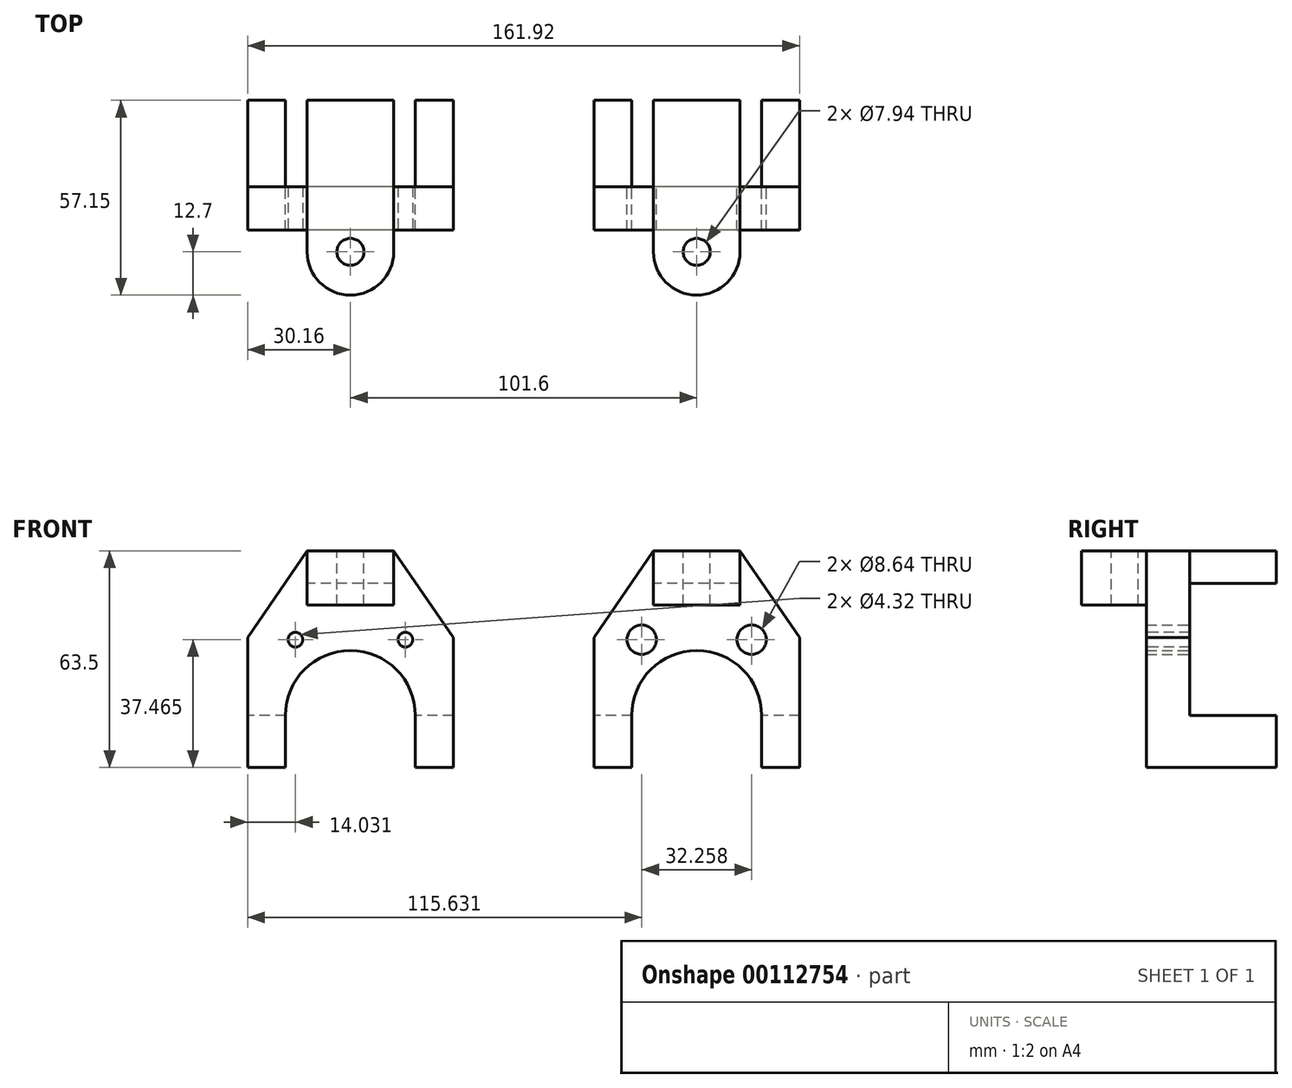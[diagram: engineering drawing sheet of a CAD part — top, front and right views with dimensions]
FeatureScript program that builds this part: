
annotation { "Feature Type Name" : "Feature", "Feature Type Description" : "" }
export const myFeature = defineFeature(function(context is Context, id is Id, definition is map)
    precondition{}
    {
        {
            var Q0;
            Q0=qCreatedBy(makeId("Front.planeOp"),FACE);
            var sketch = newSketch(context, id + "F0", { "sketchPlane" : qUnion([Q0])});
            skLineSegment(sketch, "E0.bottom", {"start": v(30.16, -31.75) * mm, "end": v(19.05, -31.75) * mm});
            skLineSegment(sketch, "E0.top", {"start": v(12.7, 31.75) * mm, "end": v(-12.7, 31.75) * mm});
            skLineSegment(sketch, "E0.left", {"start": v(30.16, -31.75) * mm, "end": v(30.16, 6.35) * mm});
            skLineSegment(sketch, "E0.right", {"start": v(-30.16, -31.75) * mm, "end": v(-30.16, 6.35) * mm});
            skPoint(sketch, "E0.middle", {"position": v(0, 0) * mm});
            skCircle(sketch, "E1", {"center": v(-16.13, 5.71) * mm, "radius": 4.32 * mm});
            skCircle(sketch, "E2", {"center": v(16.13, 5.72) * mm, "radius": 4.32 * mm});
            skLineSegment(sketch, "E3", {"start": v(0, 0) * mm, "end": v(0, -39.85) * mm, "construction": true});
            skArc(sketch, "E4", {"start": v(19.05, -16.51) * mm, "mid": v(0, 2.54) * mm, "end": v(-19.05, -16.51) * mm});
            skLineSegment(sketch, "E5", {"start": v(-45.22, 2.54) * mm, "end": v(54.05, 2.54) * mm, "construction": true});
            skLineSegment(sketch, "E6", {"start": v(-19.05, -16.51) * mm, "end": v(-19.05, -31.75) * mm});
            skLineSegment(sketch, "E7", {"start": v(19.05, -16.51) * mm, "end": v(19.05, -31.75) * mm});
            skLineSegment(sketch, "E8.trimOffspring", {"start": v(-19.05, -31.75) * mm, "end": v(-30.16, -31.75) * mm});
            skLineSegment(sketch, "E9", {"start": v(-12.7, 31.75) * mm, "end": v(-30.16, 6.35) * mm});
            skLineSegment(sketch, "E10", {"start": v(12.7, 31.75) * mm, "end": v(30.16, 6.35) * mm});
            skPoint(sketch, "E11.orphan", {"position": v(-30.16, 31.75) * mm});
            skPoint(sketch, "E12.orphan", {"position": v(30.16, 31.75) * mm});
            skSolve(sketch);
        }
        {
            var Q0;
            Q0 = qSketchRegion(id + "F0", true);
            extrude(context, id + "F1", {"entities" : qUnion([Q0]), "depth" : 12.7 * mm});
        }
        {
            var Q0;
            Q0=makeQuery(id+"F1.opExtrude","SWEPT_FACE",FACE,{"disambiguationData":[OSD([sQuery(id+"F0.wireOp",EDGE,"E0.top")])]});
            var sketch = newSketch(context, id + "F2", { "sketchPlane" : qUnion([Q0])});
            skCircle(sketch, "E13", {"center": v(0, -19.05) * mm, "radius": 3.97 * mm});
            skArc(sketch, "E14", {"start": v(-12.7, -19.05) * mm, "mid": v(0, -31.75) * mm, "end": v(12.7, -19.05) * mm});
            skLineSegment(sketch, "E15", {"start": v(-12.7, -19.05) * mm, "end": v(-12.7, 0) * mm});
            skLineSegment(sketch, "E16", {"start": v(12.7, -19.05) * mm, "end": v(12.7, 0) * mm});
            skLineSegment(sketch, "E17", {"start": v(12.7, 0) * mm, "end": v(-12.7, 0) * mm});
            skSolve(sketch);
        }
        {
            var Q0;
            Q0 = qSketchRegion(id + "F2", true);
            extrude(context, id + "F3", {"entities" : qUnion([Q0]), "operationType" : NewBodyOperationType.ADD, "oppositeDirection" : true, "depth" : 15.88 * mm});
        }
        {
            var Q0;
            Q0=makeQuery(id+"F1.opExtrude","CAP_FACE",FACE,{"disambiguationData":[OSD([sQuery(id+"F0.wireOp",EDGE,"E0.bottom"),sQuery(id+"F0.wireOp",EDGE,"E0.top"),sQuery(id+"F0.wireOp",EDGE,"E0.left"),sQuery(id+"F0.wireOp",EDGE,"E0.right"),sQuery(id+"F0.wireOp",EDGE,"E1"),sQuery(id+"F0.wireOp",EDGE,"E2"),sQuery(id+"F0.wireOp",EDGE,"E4"),sQuery(id+"F0.wireOp",EDGE,"E6"),sQuery(id+"F0.wireOp",EDGE,"E7"),sQuery(id+"F0.wireOp",EDGE,"E8.trimOffspring"),sQuery(id+"F0.wireOp",EDGE,"E9"),sQuery(id+"F0.wireOp",EDGE,"E10")])],"isStart":true});
            var sketch = newSketch(context, id + "F4", { "sketchPlane" : qUnion([Q0])});
            skLineSegment(sketch, "E18.bottom", {"start": v(-12.7, 31.75) * mm, "end": v(12.7, 31.75) * mm});
            skLineSegment(sketch, "E18.top", {"start": v(-12.7, 22.23) * mm, "end": v(12.7, 22.23) * mm});
            skLineSegment(sketch, "E18.left", {"start": v(-12.7, 31.75) * mm, "end": v(-12.7, 22.23) * mm});
            skLineSegment(sketch, "E18.right", {"start": v(12.7, 31.75) * mm, "end": v(12.7, 22.23) * mm});
            skLineSegment(sketch, "E19.bottom", {"start": v(-30.16, -31.75) * mm, "end": v(-19.05, -31.75) * mm});
            skLineSegment(sketch, "E19.top", {"start": v(-30.16, -16.51) * mm, "end": v(-19.05, -16.51) * mm});
            skLineSegment(sketch, "E19.left", {"start": v(-30.16, -31.75) * mm, "end": v(-30.16, -16.51) * mm});
            skLineSegment(sketch, "E19.right", {"start": v(-19.05, -31.75) * mm, "end": v(-19.05, -16.51) * mm});
            skLineSegment(sketch, "E20.bottom", {"start": v(19.05, -31.75) * mm, "end": v(30.16, -31.75) * mm});
            skLineSegment(sketch, "E20.top", {"start": v(19.05, -16.51) * mm, "end": v(30.16, -16.51) * mm});
            skLineSegment(sketch, "E20.left", {"start": v(19.05, -31.75) * mm, "end": v(19.05, -16.51) * mm});
            skLineSegment(sketch, "E20.right", {"start": v(30.16, -31.75) * mm, "end": v(30.16, -16.51) * mm});
            skSolve(sketch);
        }
        {
            var Q0;
            Q0 = qSketchRegion(id + "F4", true);
            extrude(context, id + "F5", {"entities" : qUnion([Q0]), "operationType" : NewBodyOperationType.ADD, "depth" : 25.4 * mm});
        }
        {
            var Q0;
            Q0=makeQuery(id+"F1.opExtrude","SWEPT_BODY",BODY,{"disambiguationData":[OSD([sQuery(id+"F0.wireOp",EDGE,"E0.bottom"),sQuery(id+"F0.wireOp",EDGE,"E0.top"),sQuery(id+"F0.wireOp",EDGE,"E0.left"),sQuery(id+"F0.wireOp",EDGE,"E0.right"),sQuery(id+"F0.wireOp",EDGE,"E1"),sQuery(id+"F0.wireOp",EDGE,"E2"),sQuery(id+"F0.wireOp",EDGE,"E4"),sQuery(id+"F0.wireOp",EDGE,"E6"),sQuery(id+"F0.wireOp",EDGE,"E7"),sQuery(id+"F0.wireOp",EDGE,"E8.trimOffspring"),sQuery(id+"F0.wireOp",EDGE,"E9"),sQuery(id+"F0.wireOp",EDGE,"E10")])]});
            transform(context, id + "F6", {"entities" : qUnion([Q0]), "transformType" : TransformType.TRANSLATION_3D, "dx" : 101.6 * mm, "dy" : 0 * mm, "dz" : 0 * mm, "makeCopy" : true});
        }
        {
            var Q0;
            Q0=makeQuery(id+"F0.imprint","IMPRINT",FACE,{"disambiguationData":[TD([[makeQuery(id+"F0.imprint","IMPRINT",EDGE,{"derivedFrom":sQuery(id+"F0.wireOp",EDGE,"E0.bottom")}),-1.0]])]});
            var sketch = newSketch(context, id + "F7", { "sketchPlane" : qUnion([Q0])});
            skCircle(sketch, "E21", {"center": v(16.13, 5.72) * mm, "radius": 4.32 * mm});
            skCircle(sketch, "E22", {"center": v(-16.13, 5.71) * mm, "radius": 4.32 * mm});
            skSolve(sketch);
        }
        {
            var Q0;
            Q0 = qSketchRegion(id + "F7", true);
            var Q1;
            Q1=makeQuery(id+"F1.opExtrude","CAP_FACE",FACE,{"disambiguationData":[OSD([sQuery(id+"F0.wireOp",EDGE,"E0.bottom"),sQuery(id+"F0.wireOp",EDGE,"E0.top"),sQuery(id+"F0.wireOp",EDGE,"E0.left"),sQuery(id+"F0.wireOp",EDGE,"E0.right"),sQuery(id+"F0.wireOp",EDGE,"E1"),sQuery(id+"F0.wireOp",EDGE,"E2"),sQuery(id+"F0.wireOp",EDGE,"E4"),sQuery(id+"F0.wireOp",EDGE,"E6"),sQuery(id+"F0.wireOp",EDGE,"E7"),sQuery(id+"F0.wireOp",EDGE,"E8.trimOffspring"),sQuery(id+"F0.wireOp",EDGE,"E9"),sQuery(id+"F0.wireOp",EDGE,"E10")])],"isStart":false});
            extrude(context, id + "F8", {"entities" : qUnion([Q0]), "operationType" : NewBodyOperationType.ADD, "endBound" : BoundingType.UP_TO_SURFACE, "endBoundEntityFace" : qUnion([Q1]), "depth" : 25.4 * mm});
        }
        {
            var Q0;
            {var subQ0=sQuery(id+"F0.wireOp",EDGE,"E10");var subQ1=sQuery(id+"F0.wireOp",EDGE,"E9");var subQ2=sQuery(id+"F0.wireOp",EDGE,"E8.trimOffspring");var subQ3=sQuery(id+"F0.wireOp",EDGE,"E7");var subQ4=sQuery(id+"F0.wireOp",EDGE,"E6");var subQ5=sQuery(id+"F0.wireOp",EDGE,"E4");var subQ6=sQuery(id+"F0.wireOp",EDGE,"E2");var subQ7=sQuery(id+"F0.wireOp",EDGE,"E1");var subQ8=sQuery(id+"F0.wireOp",EDGE,"E0.right");var subQ9=sQuery(id+"F0.wireOp",EDGE,"E0.left");var subQ10=sQuery(id+"F0.wireOp",EDGE,"E0.top");var subQ11=sQuery(id+"F0.wireOp",EDGE,"E0.bottom");Q0=makeQuery(id+"F8.boolean.opBoolean","MERGE",FACE,{"derivedFrom":[makeQuery(id+"F1.opExtrude","CAP_FACE",FACE,{"disambiguationData":[OSD([subQ11,subQ10,subQ9,subQ8,subQ7,subQ6,subQ5,subQ4,subQ3,subQ2,subQ1,subQ0])],"isStart":false}),makeQuery(id+"F8.opExtrude","CAP_FACE",FACE,{"disambiguationData":[OSD([subQ11,subQ10,subQ9,subQ8,subQ7,subQ6,subQ5,subQ4,subQ3,subQ2,subQ1,subQ0]),ownerDisambiguation([makeQuery(id+"F8.opExtrude","SWEPT_BODY",BODY,{"disambiguationData":[OSD([sQuery(id+"F7.wireOp",EDGE,"E21")])]})])],"isStart":false}),makeQuery(id+"F8.opExtrude","CAP_FACE",FACE,{"disambiguationData":[OSD([subQ11,subQ10,subQ9,subQ8,subQ7,subQ6,subQ5,subQ4,subQ3,subQ2,subQ1,subQ0]),ownerDisambiguation([makeQuery(id+"F8.opExtrude","SWEPT_BODY",BODY,{"disambiguationData":[OSD([sQuery(id+"F7.wireOp",EDGE,"E22")])]})])],"isStart":false})]});}
            var sketch = newSketch(context, id + "F9", { "sketchPlane" : qUnion([Q0])});
            skCircle(sketch, "E23", {"center": v(-16.13, 5.71) * mm, "radius": 2.16 * mm});
            skCircle(sketch, "E24", {"center": v(16.13, 5.72) * mm, "radius": 2.16 * mm});
            skSolve(sketch);
        }
        {
            var Q0;
            Q0 = qSketchRegion(id + "F9", true);
            extrude(context, id + "F10", {"entities" : qUnion([Q0]), "operationType" : NewBodyOperationType.REMOVE, "endBound" : BoundingType.THROUGH_ALL, "oppositeDirection" : true, "depth" : 12.7 * mm});
        }
    });
